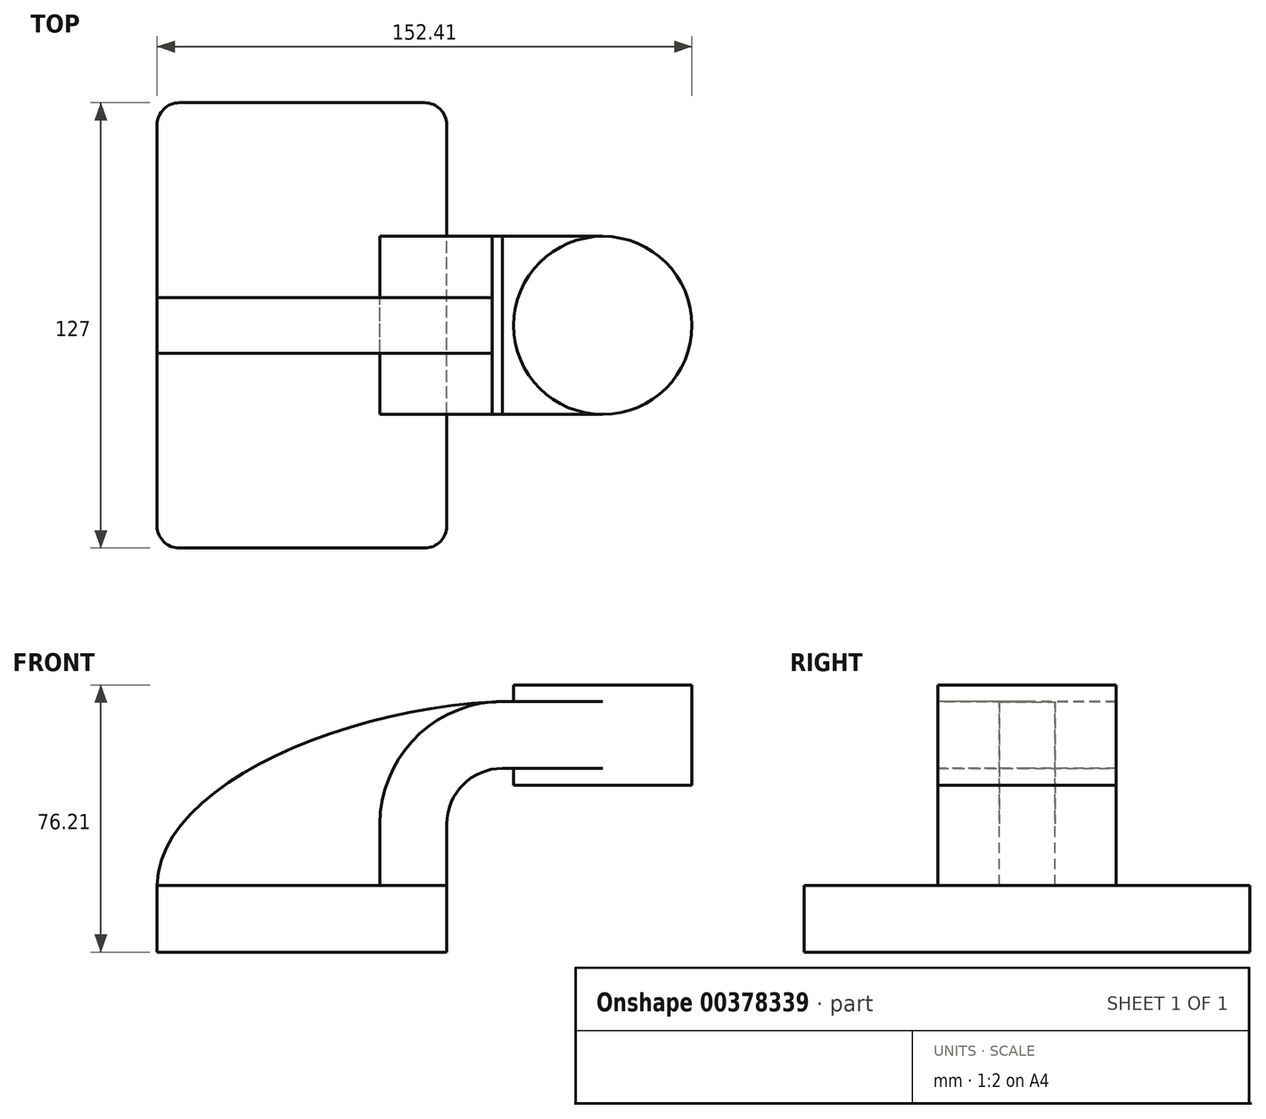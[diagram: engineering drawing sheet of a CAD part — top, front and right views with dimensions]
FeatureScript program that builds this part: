
annotation { "Feature Type Name" : "Feature", "Feature Type Description" : "" }
export const myFeature = defineFeature(function(context is Context, id is Id, definition is map)
    precondition{}
    {
        {
            var Q0;
            Q0=qCreatedBy(makeId("Front.planeOp"),FACE);
            var sketch = newSketch(context, id + "F0", { "sketchPlane" : qUnion([Q0])});
            skLineSegment(sketch, "E0.bottom", {"start": v(-41.28, -9.52) * mm, "end": v(41.28, -9.52) * mm});
            skLineSegment(sketch, "E0.top", {"start": v(-41.28, 9.52) * mm, "end": v(41.28, 9.52) * mm});
            skLineSegment(sketch, "E0.left", {"start": v(-41.28, -9.52) * mm, "end": v(-41.28, 9.52) * mm});
            skLineSegment(sketch, "E0.right", {"start": v(41.28, -9.53) * mm, "end": v(41.28, 9.52) * mm});
            skPoint(sketch, "E0.middle", {"position": v(0, 0) * mm});
            skLineSegment(sketch, "E1.bottom", {"start": v(60.33, 38.1) * mm, "end": v(111.12, 38.1) * mm});
            skLineSegment(sketch, "E1.top", {"start": v(60.32, 66.67) * mm, "end": v(111.12, 66.67) * mm});
            skLineSegment(sketch, "E1.left", {"start": v(60.33, 38.1) * mm, "end": v(60.32, 66.67) * mm});
            skLineSegment(sketch, "E1.right", {"start": v(111.12, 38.1) * mm, "end": v(111.12, 66.68) * mm});
            skPoint(sketch, "E1.middle", {"position": v(85.72, 52.39) * mm});
            skLineSegment(sketch, "E2", {"start": v(41.27, 9.52) * mm, "end": v(41.27, 27) * mm});
            skArc(sketch, "E3", {"start": v(41.27, 27) * mm, "mid": v(45.92, 38.23) * mm, "end": v(57.15, 42.88) * mm});
            skLineSegment(sketch, "E4", {"start": v(57.15, 42.88) * mm, "end": v(85.72, 42.88) * mm});
            skLineSegment(sketch, "E5.0", {"start": v(57.15, 61.93) * mm, "end": v(85.72, 61.93) * mm});
            skArc(sketch, "E5.1", {"start": v(22.23, 27) * mm, "mid": v(32.45, 51.7) * mm, "end": v(57.15, 61.93) * mm});
            skLineSegment(sketch, "E5.2", {"start": v(22.22, 9.52) * mm, "end": v(22.22, 27) * mm});
            skLineSegment(sketch, "E6", {"start": v(85.72, 38.1) * mm, "end": v(85.72, 66.67) * mm});
            skFitSpline(sketch, "E7", {"points": [v(-41.28, 9.53) * mm, v(57.15, 61.93) * mm], "startDerivative": vector(0.92, 85.64) * mm, "endDerivative": vector(133.88, 4.39) * mm});
            skSolve(sketch);
        }
        {
            var Q0;
            Q0=makeQuery(id+"F0.imprint","IMPRINT",FACE,{"disambiguationData":[TD([[makeQuery(id+"F0.imprint","IMPRINT",EDGE,{"derivedFrom":sQuery(id+"F0.wireOp",EDGE,"E0.bottom")}),1.0]])]});
            var Q1;
            Q1=sQuery(id+"F0.wireOp",EDGE,"E7");
            extrude(context, id + "F1", {"entities" : qUnion([Q0]), "surfaceEntities" : qUnion([Q1]), "endBound" : BoundingType.SYMMETRIC, "depth" : 127 * mm});
        }
        {
            var Q0;
            {var subQ1=sQuery(id+"F0.wireOp",EDGE,"E2");Q0=makeQuery(id+"F0.imprint","IMPRINT",FACE,{"disambiguationData":[TD([[makeQuery(id+"F0.imprint","IMPRINT",EDGE,{"derivedFrom":subQ1}),1.0]])]});}
            var Q1;
            {var subQ0=sQuery(id+"F0.wireOp",EDGE,"E4");var subQ1=sQuery(id+"F0.wireOp",EDGE,"E1.left");var subQ2=makeQuery(id+"F0.imprint","INTERSECT",VERTEX,{"derivedFrom":[subQ1,subQ0]});Q1=makeQuery(id+"F0.imprint","IMPRINT",FACE,{"disambiguationData":[TD([[makeQuery(id+"F0.imprint","IMPRINT",EDGE,{"disambiguationData":[TD([[subQ2,-1.0]])],"derivedFrom":subQ1}),-1.0]])]});}
            extrude(context, id + "F2", {"entities" : qUnion([Q0, Q1]), "endBound" : BoundingType.SYMMETRIC, "depth" : 50.8 * mm});
        }
        {
            var Q0;
            {var subQ3=sQuery(id+"F0.wireOp",EDGE,"E5.2");Q0=makeQuery(id+"F0.imprint","IMPRINT",FACE,{"disambiguationData":[TD([[makeQuery(id+"F0.imprint","IMPRINT",EDGE,{"derivedFrom":subQ3}),1.0]])]});}
            extrude(context, id + "F3", {"entities" : qUnion([Q0]), "endBound" : BoundingType.SYMMETRIC, "depth" : 15.88 * mm});
        }
        {
            var Q0;
            {var subQ4=sQuery(id+"F0.wireOp",EDGE,"E1.right");Q0=makeQuery(id+"F0.imprint","IMPRINT",FACE,{"disambiguationData":[TD([[makeQuery(id+"F0.imprint","IMPRINT",EDGE,{"derivedFrom":subQ4}),1.0]])]});}
            var Q1;
            Q1=sQuery(id+"F0.wireOp",EDGE,"E6");
            revolve(context, id + "F4", {"operationType" : NewBodyOperationType.ADD, "entities" : qUnion([Q0]), "axis" : qUnion([Q1]), "revolveType" : RevolveType.FULL});
        }
        {
            var Q0;
            Q0=makeQuery(id+"F1.opExtrude","CAP_EDGE",EDGE,{"disambiguationData":[OSD([sQuery(id+"F0.wireOp",EDGE,"E0.right")])],"isStart":false});
            var Q1;
            Q1=makeQuery(id+"F1.opExtrude","CAP_EDGE",EDGE,{"disambiguationData":[OSD([sQuery(id+"F0.wireOp",EDGE,"E0.right")])],"isStart":true});
            var Q2;
            Q2=makeQuery(id+"F1.opExtrude","CAP_EDGE",EDGE,{"disambiguationData":[OSD([sQuery(id+"F0.wireOp",EDGE,"E0.left")])],"isStart":true});
            var Q3;
            Q3=makeQuery(id+"F1.opExtrude","CAP_EDGE",EDGE,{"disambiguationData":[OSD([sQuery(id+"F0.wireOp",EDGE,"E0.left")])],"isStart":false});
            fillet(context, id + "F5", {"entities" : qUnion([Q0, Q1, Q2, Q3]), "radius" : 6.35 * mm, "tangentPropagation" : true, "allowEdgeOverflow" : false});
        }
    });
